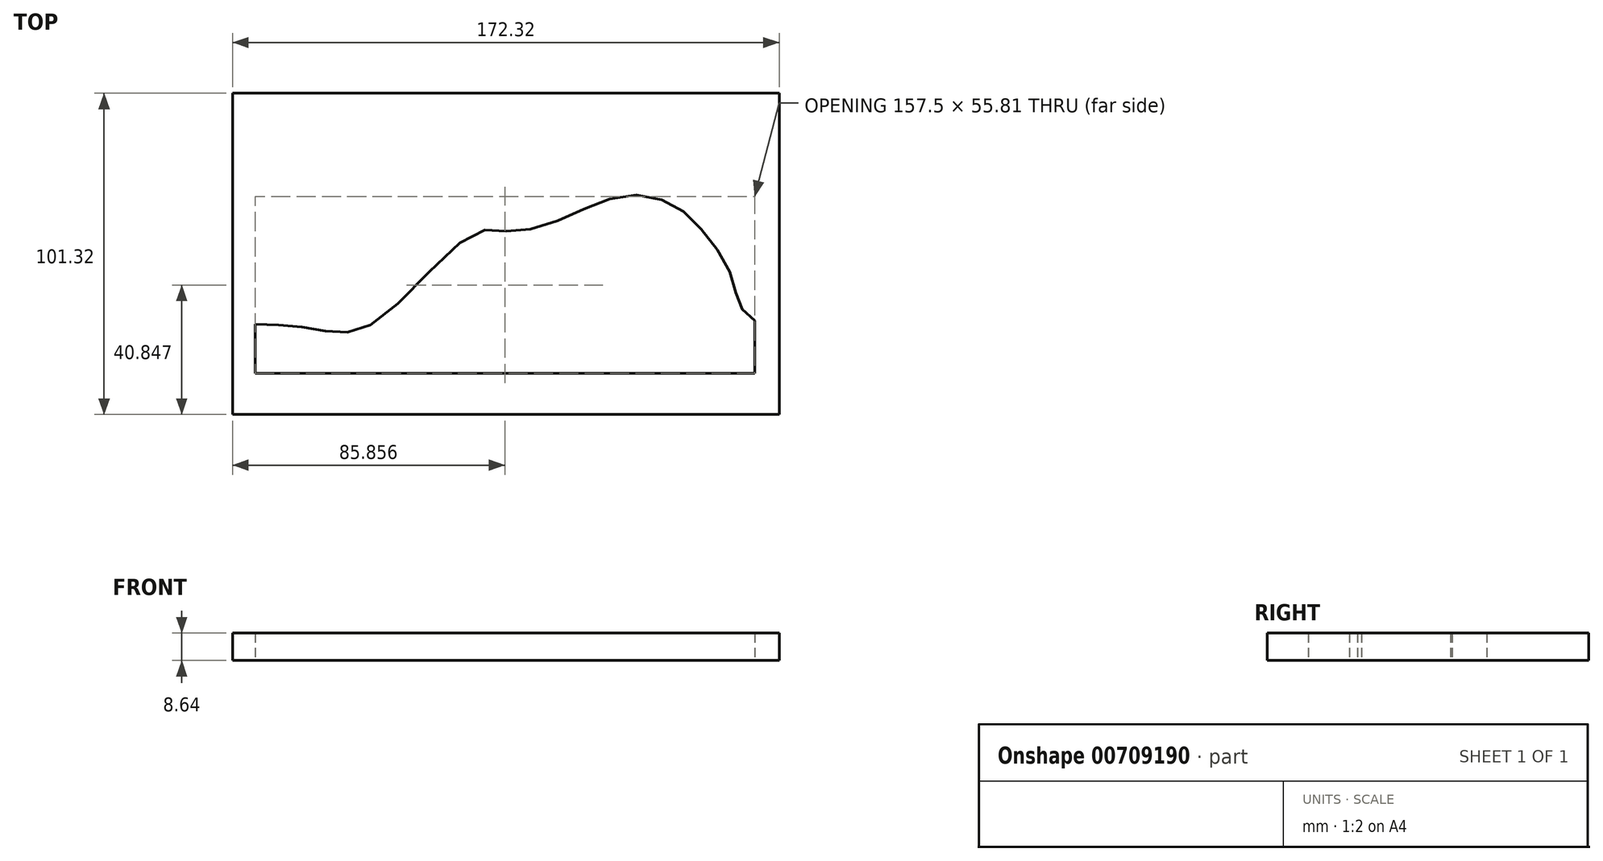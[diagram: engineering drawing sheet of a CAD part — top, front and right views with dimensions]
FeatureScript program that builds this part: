
annotation { "Feature Type Name" : "Feature", "Feature Type Description" : "" }
export const myFeature = defineFeature(function(context is Context, id is Id, definition is map)
    precondition{}
    {
        {
            var Q0;
            Q0=qCreatedBy(makeId("Top.planeOp"),FACE);
            var sketch = newSketch(context, id + "F0", { "sketchPlane" : qUnion([Q0])});
            skFitSpline(sketch, "E0", {"points": [v(-88.53, -24.3) * mm, v(-75.28, -24.93) * mm, v(-62.34, -26.83) * mm, v(-48.45, -22.1) * mm, v(-19.41, 4.42) * mm, v(-7.73, 5.05) * mm, v(9.31, 9.47) * mm, v(26.67, 16.1) * mm, v(42.45, 13.89) * mm, v(53.5, 4.1) * mm, v(61.7, -9.15) * mm, v(64.23, -18.3) * mm, v(68.96, -23.04) * mm], "startDerivative": vector(169.98, -1.05) * mm, "endDerivative": vector(100.06, -73.87) * mm});
            skLineSegment(sketch, "E1", {"start": v(-88.53, -24.3) * mm, "end": v(-88.53, -39.77) * mm});
            skLineSegment(sketch, "E2", {"start": v(-88.53, -39.77) * mm, "end": v(68.96, -39.77) * mm});
            skLineSegment(sketch, "E3", {"start": v(68.96, -39.77) * mm, "end": v(68.96, -23.04) * mm});
            skLineSegment(sketch, "E4.bottom", {"start": v(-95.64, -52.7) * mm, "end": v(76.68, -52.7) * mm});
            skLineSegment(sketch, "E4.top", {"start": v(-95.64, 48.6) * mm, "end": v(76.68, 48.6) * mm});
            skLineSegment(sketch, "E4.left", {"start": v(-95.64, -52.7) * mm, "end": v(-95.64, 48.6) * mm});
            skLineSegment(sketch, "E4.right", {"start": v(76.68, -52.7) * mm, "end": v(76.68, 48.6) * mm});
            skSolve(sketch);
        }
        {
            var Q0;
            Q0=makeQuery(id+"F0.imprint","IMPRINT",FACE,{"disambiguationData":[TD([[makeQuery(id+"F0.imprint","IMPRINT",EDGE,{"derivedFrom":sQuery(id+"F0.wireOp",EDGE,"E0")}),1.0]])]});
            extrude(context, id + "F1", {"entities" : qUnion([Q0]), "depth" : 8.64 * mm, "offsetDistance" : 25.4 * mm});
        }
    });
